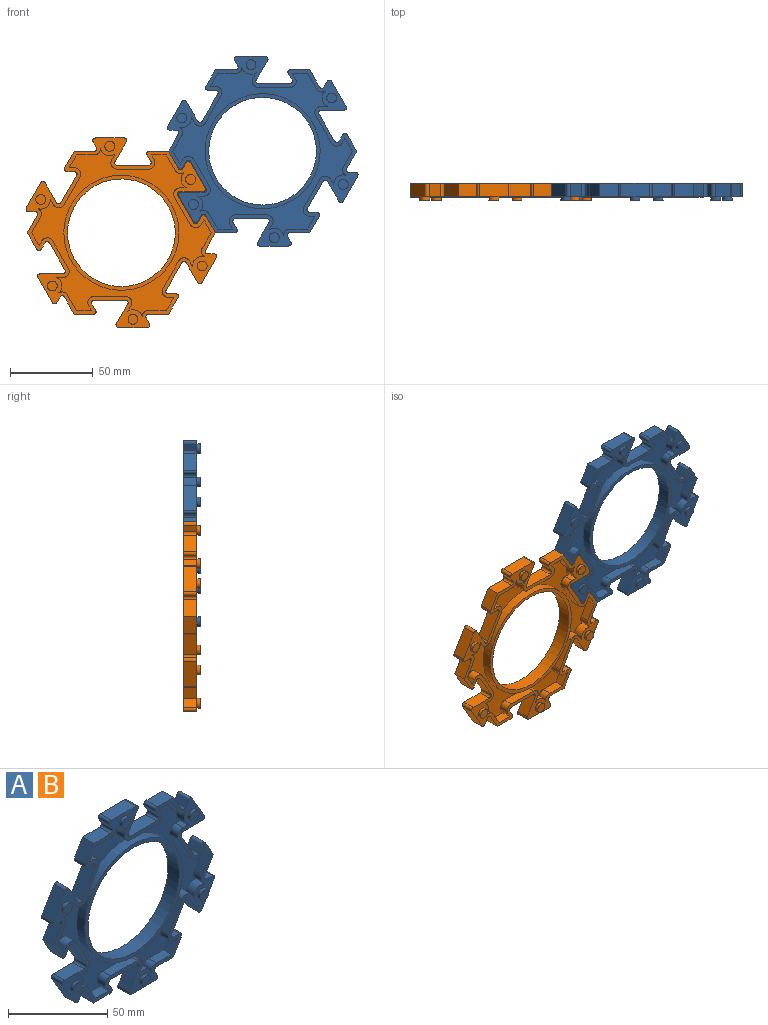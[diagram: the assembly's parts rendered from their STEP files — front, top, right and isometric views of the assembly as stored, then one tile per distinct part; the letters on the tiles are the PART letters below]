
ASSEMBLY  parts=2 mates=1
PART A: 162 faces, bbox 115.2x10x114.4 mm
  f0: plane 5.75x3.75mm, normal (0,0,1), area 21.6mm2, adj f13,f123,f124,f151
  f1: cylinder r=3.75mm len=5.75mm, axis (0,-1,0), area 34.5mm2, adj f13,f123,f124,f149
  f2: plane 5.75x3.25mm, normal (0.87,0,0.5), area 21.6mm2, adj f13,f122,f124,f153
  f3: cylinder r=3.75mm len=5.75mm, axis (0,-1,0), area 34.5mm2, adj f13,f122,f124,f145
  f4: plane 5.75x3.25mm, normal (0.87,0,-0.5), area 21.6mm2, adj f13,f121,f124,f155
  f5: cylinder r=3.75mm len=5.75mm, axis (0,-1,0), area 34.5mm2, adj f13,f121,f124,f141
  f6: plane 5.75x3.75mm, normal (0,0,-1), area 21.6mm2, adj f13,f120,f124,f157
  f7: cylinder r=3.75mm len=5.75mm, axis (0,-1,0), area 34.5mm2, adj f13,f120,f124,f137
  f8: plane 5.75x3.25mm, normal (-0.87,0,-0.5), area 21.6mm2, adj f13,f119,f124,f159
  f9: cylinder r=3.75mm len=5.75mm, axis (0,-1,0), area 34.5mm2, adj f13,f119,f124,f133
  f10: plane 5.75x3.25mm, normal (-0.87,0,0.5), area 21.6mm2, adj f13,f118,f124,f161
  f11: cylinder r=3.75mm len=5.75mm, axis (0,-1,0), area 34.5mm2, adj f13,f118,f124,f128
  f12: plane 69.5x69.5mm, normal (0,-1,0), area 475.4mm2, adj f21,f129
  f13: plane 115.22x114.43mm, normal (0,-1,0), area 1694.8mm2, adj f0,f1,f2,f3,f4,f5,f6,f7
  f14: plane 11.61x8mm, normal (0,0,1), area 92.9mm2, adj f13,f22,f77,f112
  f15: plane 8x4mm, normal (-0.87,0,-0.5), area 37mm2, adj f13,f22,f112,f113
  f16: plane 19.08x8mm, normal (0,0,1), area 152.6mm2, adj f13,f22,f113,f114
  f17: plane 12x8mm, normal (0.87,0,-0.5), area 110.9mm2, adj f13,f22,f114,f115
  f18: plane 17.5x8mm, normal (0,0,1), area 140mm2, adj f13,f22,f115,f116
  f19: plane 8x3.5mm, normal (-0.87,0,-0.5), area 32.3mm2, adj f13,f22,f116,f117
  f20: plane 12.11x8mm, normal (0,0,1), area 96.9mm2, adj f13,f22,f27,f117
  f21: cylinder r=32.5mm len=65mm, axis (0,1,0), area 1633.6mm2, adj f12,f22
  f22: plane 115.22x114.43mm, normal (0,1,0), area 4720.5mm2, adj f14,f15,f16,f17,f18,f19,f20,f21
  f23: cylinder r=3mm len=6mm, axis (0,1,0), area 37.7mm2, adj f13,f24
  f24: plane 6x6mm, normal (0,-1,0), area 28.3mm2, adj f23
  f25: cylinder r=3.5mm len=7mm, axis (0,1,0), area 55mm2, adj f22,f26
  f26: plane 7x7mm, normal (0,1,0), area 38.5mm2, adj f25
  f27: plane 10.05x8mm, normal (-0.87,0,0.5), area 92.9mm2, adj f13,f20,f22,f106
  f28: plane 8x4.62mm, normal (0,0,-1), area 37mm2, adj f13,f22,f106,f107
  f29: plane 16.52x9.54mm, normal (-0.87,0,0.5), area 152.6mm2, adj f13,f22,f107,f108
  f30: plane 12x8mm, normal (0.87,0,0.5), area 110.9mm2, adj f13,f22,f108,f109
  f31: plane 15.15x8.75mm, normal (-0.87,0,0.5), area 140mm2, adj f13,f22,f109,f110
  f32: plane 8x4.04mm, normal (0,0,-1), area 32.3mm2, adj f13,f22,f110,f111
  f33: plane 10.49x8mm, normal (-0.87,0,0.5), area 96.9mm2, adj f13,f22,f38,f111
  f34: cylinder r=3mm len=6mm, axis (0,1,0), area 37.7mm2, adj f13,f35
  f35: plane 6x6mm, normal (0,-1,0), area 28.3mm2, adj f34
  f36: cylinder r=3.5mm len=7mm, axis (0,1,0), area 55mm2, adj f22,f37
  f37: plane 7x7mm, normal (0,1,0), area 38.5mm2, adj f36
  f38: plane 10.05x8mm, normal (-0.87,0,-0.5), area 92.9mm2, adj f13,f22,f33,f100
  f39: plane 8x4mm, normal (0.87,0,-0.5), area 37mm2, adj f13,f22,f100,f101
  f40: plane 16.52x9.54mm, normal (-0.87,0,-0.5), area 152.6mm2, adj f13,f22,f101,f102
  f41: plane 13.86x8mm, normal (0,0,1), area 110.9mm2, adj f13,f22,f102,f103
  f42: plane 15.15x8.75mm, normal (-0.87,0,-0.5), area 140mm2, adj f13,f22,f103,f104
  f43: plane 8x3.5mm, normal (0.87,0,-0.5), area 32.3mm2, adj f13,f22,f104,f105
  f44: plane 10.49x8mm, normal (-0.87,0,-0.5), area 96.9mm2, adj f13,f22,f49,f105
  f45: cylinder r=3mm len=6mm, axis (0,1,0), area 37.7mm2, adj f13,f46
  f46: plane 6x6mm, normal (0,-1,0), area 28.3mm2, adj f45
  f47: cylinder r=3.5mm len=7mm, axis (0,1,0), area 55mm2, adj f22,f48
  f48: plane 7x7mm, normal (0,1,0), area 38.5mm2, adj f47
  f49: plane 11.61x8mm, normal (0,0,-1), area 92.9mm2, adj f13,f22,f44,f94
  f50: plane 8x4mm, normal (0.87,0,0.5), area 37mm2, adj f13,f22,f94,f95
  f51: plane 19.08x8mm, normal (0,0,-1), area 152.6mm2, adj f13,f22,f95,f96
  f52: plane 12x8mm, normal (-0.87,0,0.5), area 110.9mm2, adj f13,f22,f96,f97
  f53: plane 17.5x8mm, normal (0,0,-1), area 140mm2, adj f13,f22,f97,f98
  f54: plane 8x3.5mm, normal (0.87,0,0.5), area 32.3mm2, adj f13,f22,f98,f99
  f55: plane 12.11x8mm, normal (0,0,-1), area 96.9mm2, adj f13,f22,f60,f99
  f56: cylinder r=3mm len=6mm, axis (0,1,0), area 37.7mm2, adj f13,f57
  f57: plane 6x6mm, normal (0,-1,0), area 28.3mm2, adj f56
  f58: cylinder r=3.5mm len=7mm, axis (0,1,0), area 55mm2, adj f22,f59
  f59: plane 7x7mm, normal (0,1,0), area 38.5mm2, adj f58
  f60: plane 10.05x8mm, normal (0.87,0,-0.5), area 92.9mm2, adj f13,f22,f55,f88
  f61: plane 8x4.62mm, normal (0,0,1), area 37mm2, adj f13,f22,f88,f89
  f62: plane 16.52x9.54mm, normal (0.87,0,-0.5), area 152.6mm2, adj f13,f22,f89,f90
  f63: plane 12x8mm, normal (-0.87,0,-0.5), area 110.9mm2, adj f13,f22,f90,f91
  f64: plane 15.15x8.75mm, normal (0.87,0,-0.5), area 140mm2, adj f13,f22,f91,f92
  f65: plane 8x4.04mm, normal (0,0,1), area 32.3mm2, adj f13,f22,f92,f93
  f66: plane 10.49x8mm, normal (0.87,0,-0.5), area 96.9mm2, adj f13,f22,f71,f93
  f67: cylinder r=3mm len=6mm, axis (0,1,0), area 37.7mm2, adj f13,f68
  f68: plane 6x6mm, normal (0,-1,0), area 28.3mm2, adj f67
  f69: cylinder r=3.5mm len=7mm, axis (0,1,0), area 55mm2, adj f22,f70
  f70: plane 7x7mm, normal (0,1,0), area 38.5mm2, adj f69
  f71: plane 10.05x8mm, normal (0.87,0,0.5), area 92.9mm2, adj f13,f22,f66,f82
  f72: plane 8x4mm, normal (-0.87,0,0.5), area 37mm2, adj f13,f22,f82,f83
  f73: plane 16.52x9.54mm, normal (0.87,0,0.5), area 152.6mm2, adj f13,f22,f83,f84
  f74: plane 13.86x8mm, normal (0,0,-1), area 110.9mm2, adj f13,f22,f84,f85
  f75: plane 15.15x8.75mm, normal (0.87,0,0.5), area 140mm2, adj f13,f22,f85,f86
  f76: plane 8x3.5mm, normal (-0.87,0,0.5), area 32.3mm2, adj f13,f22,f86,f87
  f77: plane 10.49x8mm, normal (0.87,0,0.5), area 96.9mm2, adj f13,f14,f22,f87
  f78: cylinder r=3mm len=6mm, axis (0,1,0), area 37.7mm2, adj f13,f79
  f79: plane 6x6mm, normal (0,-1,0), area 28.3mm2, adj f78
  f80: cylinder r=3.5mm len=7mm, axis (0,1,0), area 55mm2, adj f22,f81
  f81: plane 7x7mm, normal (0,1,0), area 38.5mm2, adj f80
  f82: cylinder r=1.5mm len=8mm, axis (0,1,0), area 25.1mm2, adj f13,f22,f71,f72
  f83: cylinder r=1.5mm len=8mm, axis (0,-1,0), area 25.1mm2, adj f13,f22,f72,f73
  f84: cylinder r=1.5mm len=8mm, axis (0,1,0), area 25.1mm2, adj f13,f22,f73,f74
  f85: cylinder r=1.5mm len=8mm, axis (0,-1,0), area 25.1mm2, adj f13,f22,f74,f75
  f86: cylinder r=1.5mm len=8mm, axis (0,1,0), area 25.1mm2, adj f13,f22,f75,f76
  f87: cylinder r=1.5mm len=8mm, axis (0,-1,0), area 25.1mm2, adj f13,f22,f76,f77
  f88: cylinder r=1.5mm len=8mm, axis (0,1,0), area 25.1mm2, adj f13,f22,f60,f61
  f89: cylinder r=1.5mm len=8mm, axis (0,-1,0), area 25.1mm2, adj f13,f22,f61,f62
  f90: cylinder r=1.5mm len=8mm, axis (0,1,0), area 25.1mm2, adj f13,f22,f62,f63
  f91: cylinder r=1.5mm len=8mm, axis (0,-1,0), area 25.1mm2, adj f13,f22,f63,f64
  f92: cylinder r=1.5mm len=8mm, axis (0,1,0), area 25.1mm2, adj f13,f22,f64,f65
  f93: cylinder r=1.5mm len=8mm, axis (0,-1,0), area 25.1mm2, adj f13,f22,f65,f66
  f94: cylinder r=1.5mm len=8mm, axis (0,1,0), area 25.1mm2, adj f13,f22,f49,f50
  f95: cylinder r=1.5mm len=8mm, axis (0,-1,0), area 25.1mm2, adj f13,f22,f50,f51
  f96: cylinder r=1.5mm len=8mm, axis (0,1,0), area 25.1mm2, adj f13,f22,f51,f52
  f97: cylinder r=1.5mm len=8mm, axis (0,-1,0), area 25.1mm2, adj f13,f22,f52,f53
  f98: cylinder r=1.5mm len=8mm, axis (0,1,0), area 25.1mm2, adj f13,f22,f53,f54
  f99: cylinder r=1.5mm len=8mm, axis (0,-1,0), area 25.1mm2, adj f13,f22,f54,f55
  f100: cylinder r=1.5mm len=8mm, axis (0,1,0), area 25.1mm2, adj f13,f22,f38,f39
  f101: cylinder r=1.5mm len=8mm, axis (0,-1,0), area 25.1mm2, adj f13,f22,f39,f40
  f102: cylinder r=1.5mm len=8mm, axis (0,1,0), area 25.1mm2, adj f13,f22,f40,f41
  f103: cylinder r=1.5mm len=8mm, axis (0,-1,0), area 25.1mm2, adj f13,f22,f41,f42
  f104: cylinder r=1.5mm len=8mm, axis (0,1,0), area 25.1mm2, adj f13,f22,f42,f43
  f105: cylinder r=1.5mm len=8mm, axis (0,-1,0), area 25.1mm2, adj f13,f22,f43,f44
  f106: cylinder r=1.5mm len=8mm, axis (0,1,0), area 25.1mm2, adj f13,f22,f27,f28
  f107: cylinder r=1.5mm len=8mm, axis (0,-1,0), area 25.1mm2, adj f13,f22,f28,f29
  f108: cylinder r=1.5mm len=8mm, axis (0,1,0), area 25.1mm2, adj f13,f22,f29,f30
  f109: cylinder r=1.5mm len=8mm, axis (0,-1,0), area 25.1mm2, adj f13,f22,f30,f31
  f110: cylinder r=1.5mm len=8mm, axis (0,1,0), area 25.1mm2, adj f13,f22,f31,f32
  f111: cylinder r=1.5mm len=8mm, axis (0,-1,0), area 25.1mm2, adj f13,f22,f32,f33
  f112: cylinder r=1.5mm len=8mm, axis (0,1,0), area 25.1mm2, adj f13,f14,f15,f22
  f113: cylinder r=1.5mm len=8mm, axis (0,-1,0), area 25.1mm2, adj f13,f15,f16,f22
  f114: cylinder r=1.5mm len=8mm, axis (0,1,0), area 25.1mm2, adj f13,f16,f17,f22
  f115: cylinder r=1.5mm len=8mm, axis (0,-1,0), area 25.1mm2, adj f13,f17,f18,f22
  f116: cylinder r=1.5mm len=8mm, axis (0,1,0), area 25.1mm2, adj f13,f18,f19,f22
  f117: cylinder r=1.5mm len=8mm, axis (0,-1,0), area 25.1mm2, adj f13,f19,f20,f22
  f118: cylinder r=5.75mm len=8.62mm, axis (0,1,0), area 62.3mm2, adj f10,f11,f13,f124
  f119: cylinder r=5.75mm len=7.33mm, axis (0,1,0), area 62.3mm2, adj f8,f9,f13,f124
  f120: cylinder r=5.75mm len=9.21mm, axis (0,1,0), area 62.3mm2, adj f6,f7,f13,f124
  f121: cylinder r=5.75mm len=8.62mm, axis (0,1,0), area 62.3mm2, adj f4,f5,f13,f124
  f122: cylinder r=5.75mm len=7.33mm, axis (0,1,0), area 62.3mm2, adj f2,f3,f13,f124
  f123: cylinder r=5.75mm len=9.21mm, axis (0,1,0), area 62.3mm2, adj f0,f1,f13,f124
  f124: plane 108.46x101.63mm, normal (0,-1,0), area 2611.5mm2, adj f0,f1,f2,f3,f4,f5,f6,f7
  f125: plane 9.01x5.75mm, normal (0,0,-1), area 51.8mm2, adj f13,f124,f126,f149
  f126: plane 5.75x2.88mm, normal (0.87,0,0.5), area 19.1mm2, adj f13,f124,f125,f160
  f127: plane 19.08x5.75mm, normal (0,0,-1), area 109.7mm2, adj f13,f124,f160,f161
  f128: plane 10.81x5.75mm, normal (0,0,-1), area 62.2mm2, adj f11,f13,f124,f130
  f129: cylinder r=34.75mm len=69.5mm, axis (0,1,0), area 1255.5mm2, adj f12,f124
  f130: plane 7.8x5.75mm, normal (0.87,0,-0.5), area 51.8mm2, adj f13,f124,f128,f131
  f131: plane 5.75x3.32mm, normal (0,0,1), area 19.1mm2, adj f13,f124,f130,f158
  f132: plane 16.52x9.54mm, normal (0.87,0,-0.5), area 109.7mm2, adj f13,f124,f158,f159
  f133: plane 9.36x5.75mm, normal (0.87,0,-0.5), area 62.2mm2, adj f9,f13,f124,f134
  f134: plane 7.8x5.75mm, normal (0.87,0,0.5), area 51.8mm2, adj f13,f124,f133,f135
  f135: plane 5.75x2.88mm, normal (-0.87,0,0.5), area 19.1mm2, adj f13,f124,f134,f156
  f136: plane 16.52x9.54mm, normal (0.87,0,0.5), area 109.7mm2, adj f13,f124,f156,f157
  f137: plane 9.36x5.75mm, normal (0.87,0,0.5), area 62.2mm2, adj f7,f13,f124,f138
  f138: plane 9.01x5.75mm, normal (0,0,1), area 51.8mm2, adj f13,f124,f137,f139
  f139: plane 5.75x2.88mm, normal (-0.87,0,-0.5), area 19.1mm2, adj f13,f124,f138,f154
  f140: plane 19.08x5.75mm, normal (0,0,1), area 109.7mm2, adj f13,f124,f154,f155
  f141: plane 10.81x5.75mm, normal (0,0,1), area 62.2mm2, adj f5,f13,f124,f142
  f142: plane 7.8x5.75mm, normal (-0.87,0,0.5), area 51.8mm2, adj f13,f124,f141,f143
  f143: plane 5.75x3.32mm, normal (0,0,-1), area 19.1mm2, adj f13,f124,f142,f152
  f144: plane 16.52x9.54mm, normal (-0.87,0,0.5), area 109.7mm2, adj f13,f124,f152,f153
  f145: plane 9.36x5.75mm, normal (-0.87,0,0.5), area 62.2mm2, adj f3,f13,f124,f146
  f146: plane 7.8x5.75mm, normal (-0.87,0,-0.5), area 51.8mm2, adj f13,f124,f145,f147
  f147: plane 5.75x2.88mm, normal (0.87,0,-0.5), area 19.1mm2, adj f13,f124,f146,f150
  f148: plane 16.52x9.54mm, normal (-0.87,0,-0.5), area 109.7mm2, adj f13,f124,f150,f151
  f149: plane 9.36x5.75mm, normal (-0.87,0,-0.5), area 62.2mm2, adj f1,f13,f124,f125
  f150: cylinder r=3.75mm len=6.5mm, axis (0,-1,0), area 45.2mm2, adj f13,f124,f147,f148
  f151: cylinder r=3.75mm len=5.75mm, axis (0,1,0), area 45.2mm2, adj f0,f13,f124,f148
  f152: cylinder r=3.75mm len=5.75mm, axis (0,-1,0), area 45.2mm2, adj f13,f124,f143,f144
  f153: cylinder r=3.75mm len=6.5mm, axis (0,1,0), area 45.2mm2, adj f2,f13,f124,f144
  f154: cylinder r=3.75mm len=5.75mm, axis (0,-1,0), area 45.2mm2, adj f13,f124,f139,f140
  f155: cylinder r=3.75mm len=5.75mm, axis (0,1,0), area 45.2mm2, adj f4,f13,f124,f140
  f156: cylinder r=3.75mm len=6.5mm, axis (0,-1,0), area 45.2mm2, adj f13,f124,f135,f136
  f157: cylinder r=3.75mm len=5.75mm, axis (0,1,0), area 45.2mm2, adj f6,f13,f124,f136
  f158: cylinder r=3.75mm len=5.75mm, axis (0,-1,0), area 45.2mm2, adj f13,f124,f131,f132
  f159: cylinder r=3.75mm len=6.5mm, axis (0,1,0), area 45.2mm2, adj f8,f13,f124,f132
  f160: cylinder r=3.75mm len=5.75mm, axis (0,-1,0), area 45.2mm2, adj f13,f124,f126,f127
  f161: cylinder r=3.75mm len=5.75mm, axis (0,1,0), area 45.2mm2, adj f10,f13,f124,f127
PART B: same geometry as A
PLACE A t=(32.11,6,84.18)mm
PLACE B t=(-53.13,6,34.97)mm
MATE fastened B.f13 <-> A.f13  axis (0,-1,0) through (-24.72,-2,84.18)mm
